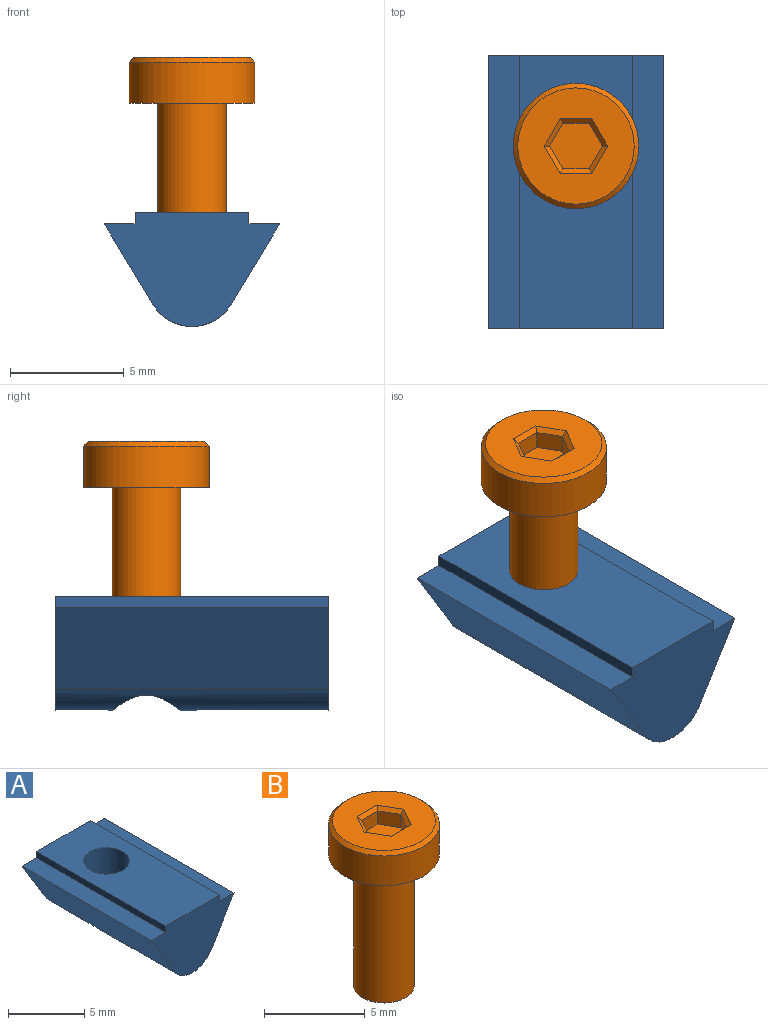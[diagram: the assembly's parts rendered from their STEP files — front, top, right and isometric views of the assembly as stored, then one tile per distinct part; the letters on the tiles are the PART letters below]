
ASSEMBLY  parts=2 mates=1
PART A: 11 faces, bbox 7.7x12x5 mm
  f0: plane 12x1.35mm, normal (0,0,1), area 16.2mm2, adj f1,f7,f8,f9
  f1: plane 12x3.54mm, normal (-0.86,0,-0.52), area 49.6mm2, adj f0,f2,f8,f9
  f2: cylinder r=2mm len=12mm, axis (0,1,0), area 41.6mm2, adj f1,f3,f8,f9,f10
  f3: plane 12x3.54mm, normal (0.86,0,-0.52), area 49.6mm2, adj f2,f4,f8,f9
  f4: plane 12x1.35mm, normal (0,0,1), area 16.2mm2, adj f3,f5,f8,f9
  f5: plane 12x0.5mm, normal (1,0,0), area 6mm2, adj f4,f6,f8,f9
  f6: plane 12x5mm, normal (0,0,1), area 52.9mm2, adj f5,f7,f8,f9,f10
  f7: plane 12x0.5mm, normal (-1,0,0), area 6mm2, adj f0,f6,f8,f9
  f8: plane 7.7x5mm, normal (0,-1,0), area 24.5mm2, adj f0,f1,f2,f3,f4,f5,f6,f7
  f9: plane 7.7x5mm, normal (0,1,0), area 24.5mm2, adj f0,f1,f2,f3,f4,f5,f6,f7
  f10: cylinder r=1.5mm len=5mm, axis (0,0,1), area 44.1mm2, adj f2,f6
PART B: 19 faces, bbox 5.5x5.5x10 mm
  f0: plane 5.1x5.1mm, normal (0,0,1), area 15.4mm2, adj f12,f13,f14,f15,f16,f17,f18
  f1: cylinder r=2.75mm len=5.5mm, axis (0,0,-1), area 31.1mm2, adj f2,f18
  f2: plane 5.5x5.5mm, normal (0,0,-1), area 16.7mm2, adj f1,f3
  f3: cylinder r=1.5mm len=8mm, axis (0,0,1), area 75.4mm2, adj f2,f4
  f4: plane 3x3mm, normal (0,0,-1), area 7.1mm2, adj f3
  f5: plane 1.15x0.8mm, normal (0,1,0), area 0.9mm2, adj f6,f10,f11,f16
  f6: plane 1x0.8mm, normal (-0.87,0.5,0), area 0.9mm2, adj f5,f7,f11,f17
  f7: plane 1x0.8mm, normal (-0.87,-0.5,0), area 0.9mm2, adj f6,f8,f11,f15
  f8: plane 1.15x0.8mm, normal (0,-1,0), area 0.9mm2, adj f7,f9,f11,f13
  f9: plane 1x0.8mm, normal (0.87,-0.5,0), area 0.9mm2, adj f8,f10,f11,f12
  f10: plane 1x0.8mm, normal (0.87,0.5,0), area 0.9mm2, adj f5,f9,f11,f14
  f11: plane 2.31x2mm, normal (0,0,1), area 3.5mm2, adj f5,f6,f7,f8,f9,f10
  f12: plane 1.2x0.81mm, normal (0.61,-0.35,0.71), area 0.4mm2, adj f0,f9,f13,f14
  f13: plane 1.39x0.2mm, normal (0,-0.71,0.71), area 0.4mm2, adj f0,f8,f12,f15
  f14: plane 1.2x0.81mm, normal (0.61,0.35,0.71), area 0.4mm2, adj f0,f10,f12,f16
  f15: plane 1.2x0.81mm, normal (-0.61,-0.35,0.71), area 0.4mm2, adj f0,f7,f13,f17
  f16: plane 1.39x0.2mm, normal (0,0.71,0.71), area 0.4mm2, adj f0,f5,f14,f17
  f17: plane 1.2x0.81mm, normal (-0.61,0.35,0.71), area 0.4mm2, adj f0,f6,f15,f16
  f18: cone r=2.55mm half-angle=45deg, axis (0,0,-1), area 4.7mm2, adj f0,f1
PLACE A t=(-1.35,-6.57,14.32)mm
PLACE B t=(-1.35,15.71,-10.38)mm
MATE fastened B.f1 <-> A.f10  axis (0,0,1) through (-1.35,-10.57,-18.38)mm
